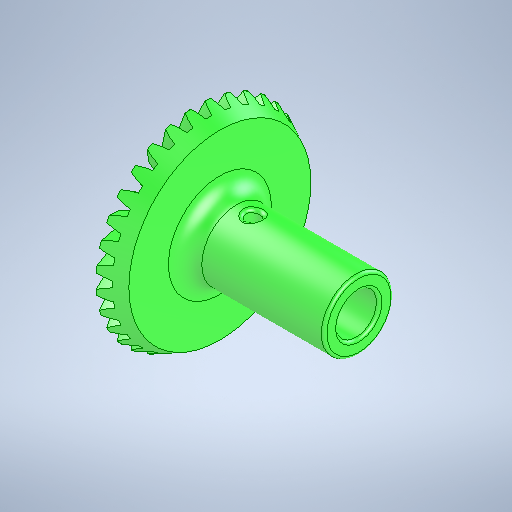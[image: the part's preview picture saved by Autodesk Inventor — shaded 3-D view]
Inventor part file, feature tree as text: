
AUTODESK INVENTOR PART (.ipt)
format: ipt  version: 2025.1 (Build 291241000, 241)  size: 763,392 bytes
history: native  units: in
note: dims shown in document units (in); Inventor stores cm internally (conversion verified against a paired STEP export)
features: sketch x8, extrude x6, plane x3, pattern_circular x2, fillet x2, revolve x1
ambient origin geometry x8: Origin, YZ Plane, XZ Plane, XY Plane, X Axis, Y Axis, Z Axis, Center Point
bodies: Solid1 (feature_tree)
feature tree (22):
  revolve  "Revolution1"  [1 undecoded]
  plane  "Work Plane7"
  extrude  "Extrusion7"  Depth=0.0945in
  plane  "Work Plane8"
  sketch  "Sketch13"  dims[d5=0.3937in d9=1.5748in]
  extrude  "Extrusion9"  Depth=0.3937in
  pattern_circular  "Circular Pattern4"  [2 undecoded]
  pattern_circular  "Circular Pattern5"  [2 undecoded]
  extrude  "Extrusion10"  Depth=0.0394in
  extrude  "Extrusion13"  Depth=0.0394in
  extrude  "Extrusion14"  Depth=0.0394in
  fillet  "Congé4"  Radius=0.0691in
  extrude  "Extrusion15"  Depth=0.0394in
  fillet  "Congé6"  Radius=0.0787in
  sketch  "Sketch1"  dims[d0=3.1496in d1=0.1825in]
  plane  "Work Plane6"
  sketch  "Sketch11"  dims[d2=0.0787in d3=0.0945in]
  sketch  "Sketch14"  dims[d10=90.0deg]
  sketch  "Sketch15"  dims[d74=0.4359in d75=0.7087in d76=0.9449in d77=1.4085in d78=0.7043in d86=-0.1825in d87=1.5748in d88=0.0691in d89=0.1374in d90=0.0787in d91=0.0197in d92=0.0945in d93=0.0079in d94=0.0079in d95=0.4724in d96=-0.0197in d109=0.2406in d110=-0.2406in d111=2.8171in d112=1.3386in d113=0.4724in d114=0.5906in d115=0.0in d116=2.3622in d117=360.0deg d119=12.5984in d120=360.0deg d122=1.1811in d123=0.0787in d124=0.0in d150=0.5768in d151=0.9843in d152=1.9685in d153=0.0in d154=0.4724in d155=0.1969in d156=1.9685in d157=0.0in d158=0.2362in d160=0.0in d161=0.0in d162=0.0394in d163=0.5768in]
  sketch  "Esquisse20"
  sketch  "Esquisse21"
  sketch  "Esquisse22"
note: 5 required parameter values undecoded (feature->parameter linkage not recoverable at this tier; creation-order binding heuristic only, values carry confidence <= 0.55)